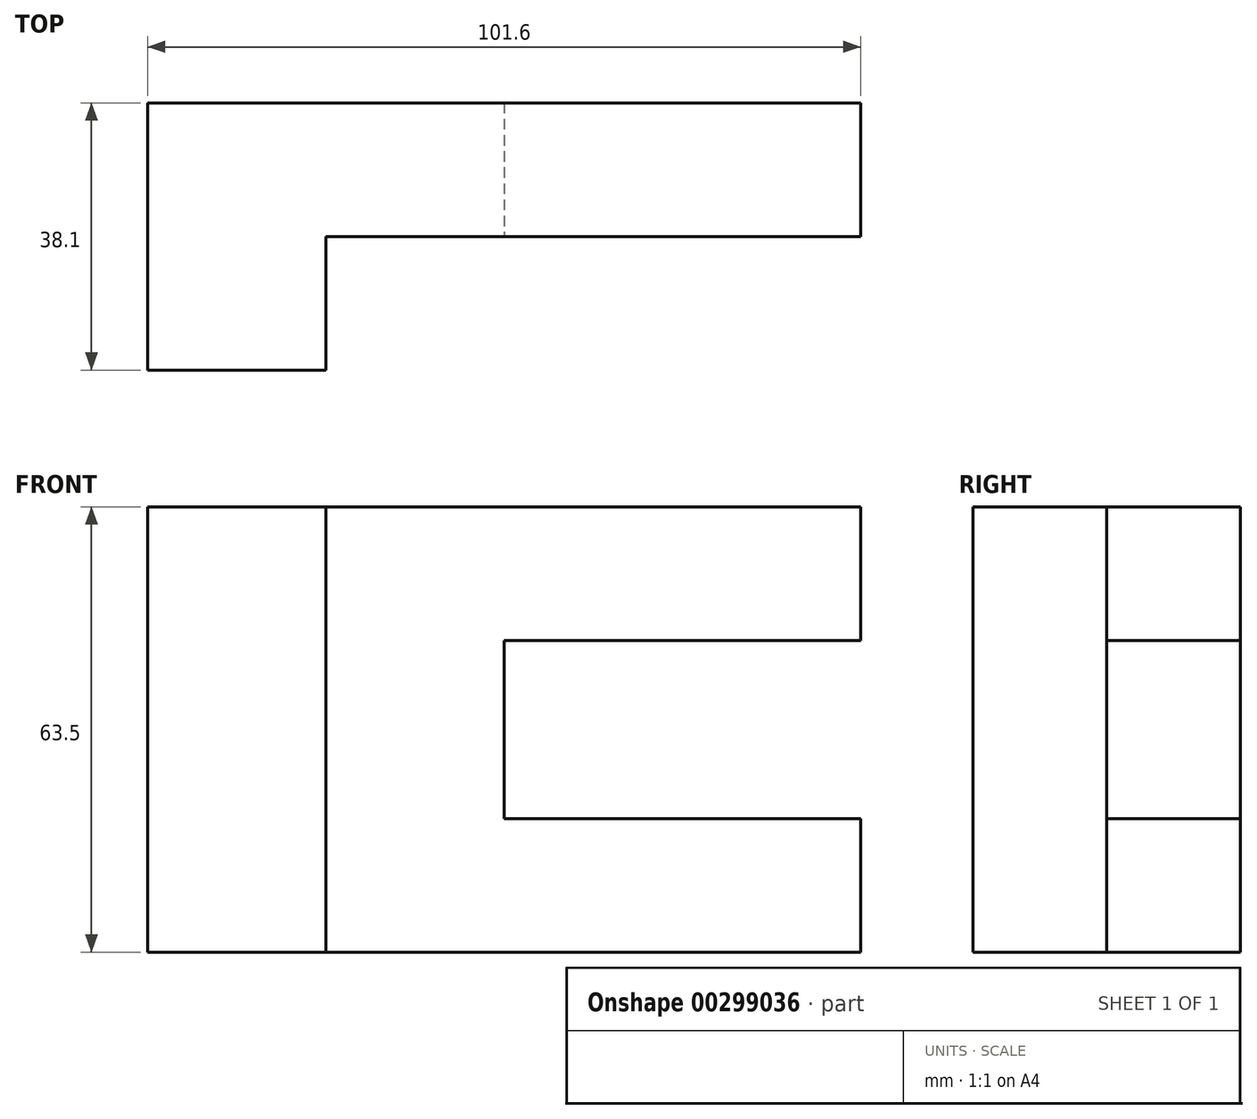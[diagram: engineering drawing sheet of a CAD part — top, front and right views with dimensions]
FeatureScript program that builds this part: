
annotation { "Feature Type Name" : "Feature", "Feature Type Description" : "" }
export const myFeature = defineFeature(function(context is Context, id is Id, definition is map)
    precondition{}
    {
        {
            var Q0;
            Q0=qCreatedBy(makeId("Front.planeOp"),FACE);
            var sketch = newSketch(context, id + "F0", { "sketchPlane" : qUnion([Q0])});
            skLineSegment(sketch, "E0.bottom", {"start": v(-50.8, 31.75) * mm, "end": v(50.8, 31.75) * mm});
            skLineSegment(sketch, "E0.top", {"start": v(-50.8, -31.75) * mm, "end": v(50.8, -31.75) * mm});
            skLineSegment(sketch, "E0.left", {"start": v(-50.8, 31.75) * mm, "end": v(-50.8, -31.75) * mm});
            skLineSegment(sketch, "E0.right", {"start": v(50.8, 31.75) * mm, "end": v(50.8, -31.75) * mm});
            skPoint(sketch, "E0.middle", {"position": v(0, 0) * mm});
            skSolve(sketch);
        }
        {
            var Q0;
            Q0=makeQuery(id+"F0.imprint","IMPRINT",FACE,{"disambiguationData":[TD([[makeQuery(id+"F0.imprint","IMPRINT",EDGE,{"derivedFrom":sQuery(id+"F0.wireOp",EDGE,"E0.bottom")}),-1.0]])]});
            extrude(context, id + "F1", {"entities" : qUnion([Q0]), "depth" : 38.1 * mm});
        }
        {
            var Q0;
            Q0=makeQuery(id+"F1.opExtrude","CAP_FACE",FACE,{"disambiguationData":[OSD([sQuery(id+"F0.wireOp",EDGE,"E0.bottom"),sQuery(id+"F0.wireOp",EDGE,"E0.top"),sQuery(id+"F0.wireOp",EDGE,"E0.left"),sQuery(id+"F0.wireOp",EDGE,"E0.right")])],"isStart":false});
            var sketch = newSketch(context, id + "F2", { "sketchPlane" : qUnion([Q0])});
            skLineSegment(sketch, "E1", {"start": v(-25.4, 31.75) * mm, "end": v(-25.4, -31.75) * mm});
            skLineSegment(sketch, "E2.top", {"start": v(50.8, -12.7) * mm, "end": v(0, -12.7) * mm});
            skLineSegment(sketch, "E2.left", {"start": v(50.8, 12.7) * mm, "end": v(50.8, -12.7) * mm});
            skLineSegment(sketch, "E2.right", {"start": v(0, 12.7) * mm, "end": v(0, -12.7) * mm});
            skLineSegment(sketch, "E3", {"start": v(0, 12.7) * mm, "end": v(50.8, 12.7) * mm});
            skSolve(sketch);
        }
        {
            var Q0;
            Q0=makeQuery(id+"F2.imprint","IMPRINT",FACE,{"disambiguationData":[TD([[makeQuery(id+"F2.imprint","IMPRINT",EDGE,{"derivedFrom":sQuery(id+"F2.wireOp",EDGE,"E2.top")}),-1.0]])]});
            extrude(context, id + "F3", {"entities" : qUnion([Q0]), "operationType" : NewBodyOperationType.REMOVE, "endBound" : BoundingType.THROUGH_ALL, "oppositeDirection" : true, "depth" : 25.4 * mm});
        }
        {
            var Q0;
            Q0 = qSketchRegion(id + "F2", true);
            var Q1;
            {var subQ2=sQuery(id+"F2.wireOp",EDGE,"E1");Q1=makeQuery(id+"F2.imprint","IMPRINT",FACE,{"disambiguationData":[TD([[makeQuery(id+"F2.imprint","IMPRINT",EDGE,{"derivedFrom":subQ2}),1.0]])]});}
            extrude(context, id + "F4", {"entities" : qUnion([Q0, Q1]), "operationType" : NewBodyOperationType.REMOVE, "oppositeDirection" : true, "depth" : 19.05 * mm});
        }
    });
